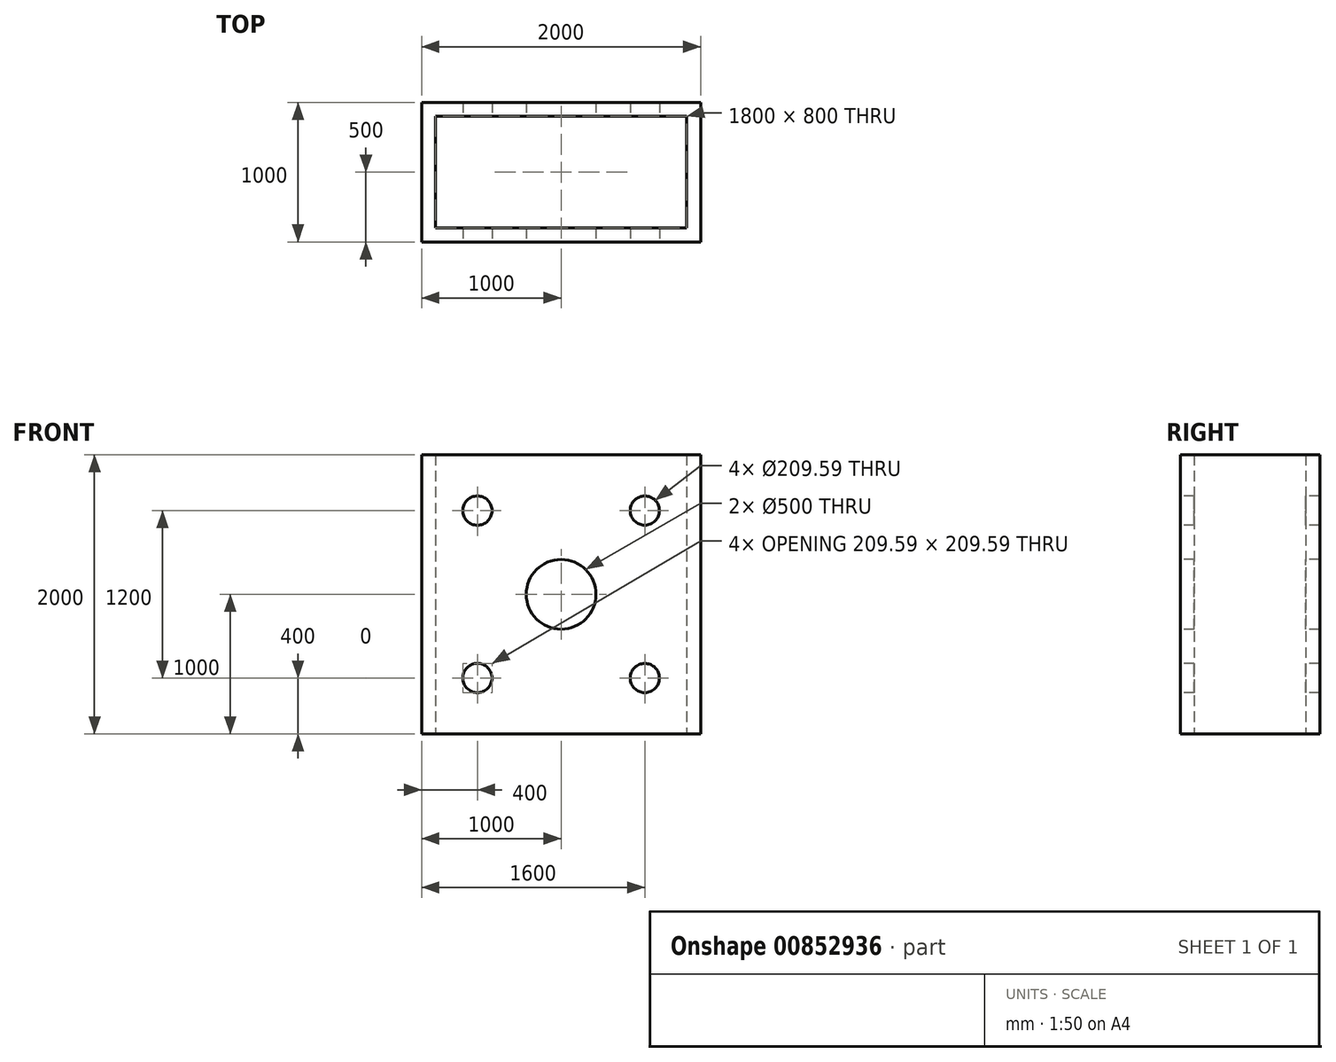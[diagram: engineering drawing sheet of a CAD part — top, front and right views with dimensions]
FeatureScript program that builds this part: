
annotation { "Feature Type Name" : "Feature", "Feature Type Description" : "" }
export const myFeature = defineFeature(function(context is Context, id is Id, definition is map)
    precondition{}
    {
        {
            var Q0;
            Q0=qCreatedBy(makeId("Top.planeOp"),FACE);
            var sketch = newSketch(context, id + "F0", { "sketchPlane" : qUnion([Q0])});
            skLineSegment(sketch, "E0.bottom", {"start": v(1000, -500) * mm, "end": v(-1000, -500) * mm});
            skLineSegment(sketch, "E0.top", {"start": v(1000, 500) * mm, "end": v(-1000, 500) * mm});
            skLineSegment(sketch, "E0.left", {"start": v(1000, -500) * mm, "end": v(1000, 500) * mm});
            skLineSegment(sketch, "E0.right", {"start": v(-1000, -500) * mm, "end": v(-1000, 500) * mm});
            skPoint(sketch, "E0.middle", {"position": v(0, 0) * mm});
            skLineSegment(sketch, "E1.0", {"start": v(-900, -400) * mm, "end": v(-900, 400) * mm});
            skLineSegment(sketch, "E1.1", {"start": v(900, -400) * mm, "end": v(-900, -400) * mm});
            skLineSegment(sketch, "E1.2", {"start": v(900, -400) * mm, "end": v(900, 400) * mm});
            skLineSegment(sketch, "E1.3", {"start": v(900, 400) * mm, "end": v(-900, 400) * mm});
            skSolve(sketch);
        }
        {
            var Q0;
            Q0=makeQuery(id+"F0.imprint","IMPRINT",FACE,{"disambiguationData":[TD([[makeQuery(id+"F0.imprint","IMPRINT",EDGE,{"derivedFrom":sQuery(id+"F0.wireOp",EDGE,"E0.bottom")}),-1.0]])]});
            extrude(context, id + "F1", {"entities" : qUnion([Q0]), "depth" : 2000 * mm, "offsetDistance" : 25 * mm});
        }
        {
            var Q0;
            Q0=makeQuery(id+"F1.opExtrude","SWEPT_FACE",FACE,{"disambiguationData":[OSD([sQuery(id+"F0.wireOp",EDGE,"E0.bottom")])]});
            var sketch = newSketch(context, id + "F2", { "sketchPlane" : qUnion([Q0])});
            skLineSegment(sketch, "E2", {"start": v(-1000, 2000) * mm, "end": v(1000, 0) * mm});
            skLineSegment(sketch, "E3", {"start": v(1000, 2000) * mm, "end": v(-1000, 0) * mm});
            skCircle(sketch, "E4", {"center": v(0, 1000) * mm, "radius": 250 * mm});
            skCircle(sketch, "E5", {"center": v(600, 1600) * mm, "radius": 104.8 * mm});
            skCircle(sketch, "E6.0.1.0", {"center": v(600, 400) * mm, "radius": 104.8 * mm});
            skCircle(sketch, "E6.1.0.0", {"center": v(-600, 1600) * mm, "radius": 104.8 * mm});
            skCircle(sketch, "E6.1.1.0", {"center": v(-600, 400) * mm, "radius": 104.8 * mm});
            skLineSegment(sketch, "E6.direction1", {"start": v(600, 1600) * mm, "end": v(-600, 1600) * mm, "construction": true});
            skLineSegment(sketch, "E6.direction2", {"start": v(600, 1600) * mm, "end": v(600, 400) * mm, "construction": true});
            skSolve(sketch);
        }
        {
            var Q0;
            Q0 = qSketchRegion(id + "F2", true);
            extrude(context, id + "F3", {"entities" : qUnion([Q0]), "operationType" : NewBodyOperationType.REMOVE, "oppositeDirection" : true, "depth" : 2225.65 * mm, "offsetDistance" : 25 * mm});
        }
        {
            var Q0;
            Q0 = qSketchRegion(id + "F2", true);
            extrude(context, id + "F4", {"entities" : qUnion([Q0]), "operationType" : NewBodyOperationType.REMOVE, "oppositeDirection" : true, "depth" : 1010.15 * mm, "offsetDistance" : 25 * mm});
        }
    });
